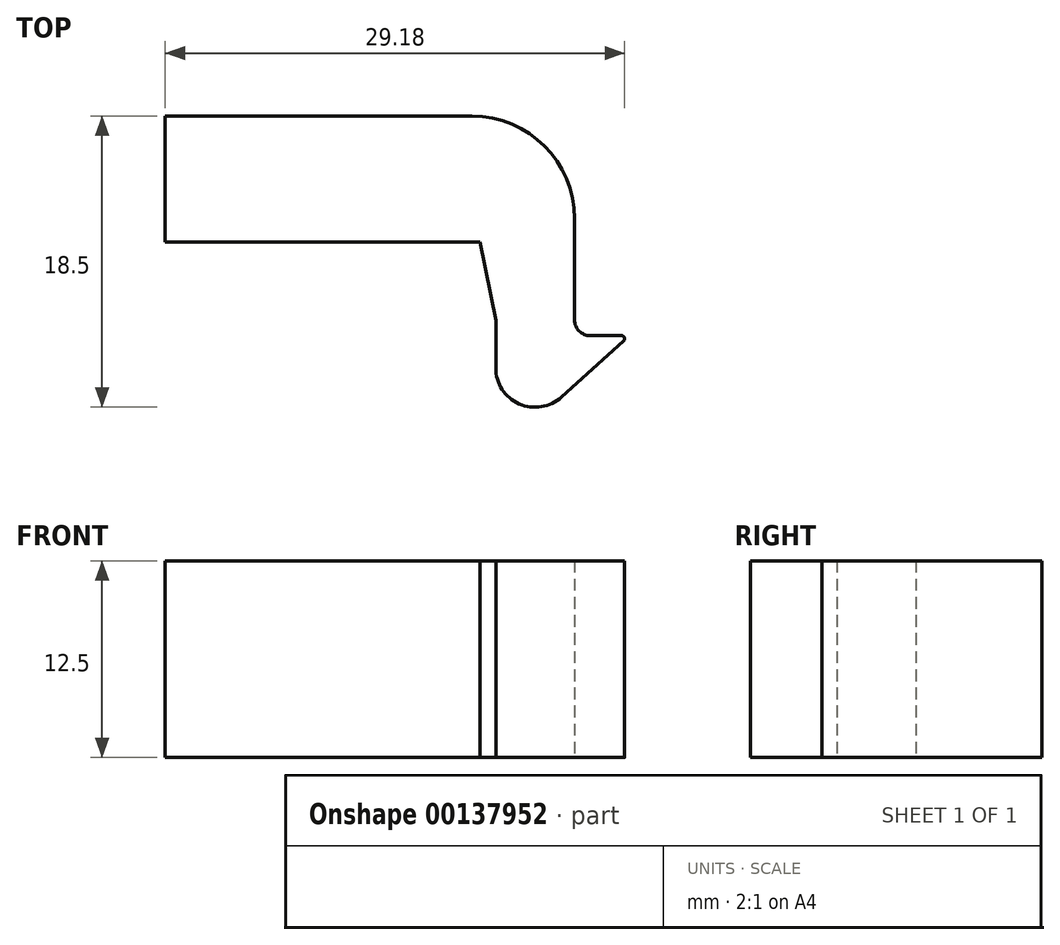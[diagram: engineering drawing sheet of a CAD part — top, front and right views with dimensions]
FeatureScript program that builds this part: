
annotation { "Feature Type Name" : "Feature", "Feature Type Description" : "" }
export const myFeature = defineFeature(function(context is Context, id is Id, definition is map)
    precondition{}
    {
        {
            var Q0;
            Q0=qCreatedBy(makeId("Top.planeOp"),FACE);
            var sketch = newSketch(context, id + "F0", { "sketchPlane" : qUnion([Q0])});
            skLineSegment(sketch, "E0.bottom", {"start": v(0, 0) * mm, "end": v(20, 0) * mm});
            skLineSegment(sketch, "E0.top", {"start": v(0, 8) * mm, "end": v(19.49, 8) * mm});
            skLineSegment(sketch, "E0.left", {"start": v(0, 0) * mm, "end": v(0, 8) * mm});
            skLineSegment(sketch, "E1", {"start": v(20, 0) * mm, "end": v(21, -5) * mm});
            skLineSegment(sketch, "E2", {"start": v(21, -5) * mm, "end": v(21, -8) * mm});
            skLineSegment(sketch, "E3", {"start": v(21, -8) * mm, "end": v(26, -8) * mm, "construction": true});
            skArc(sketch, "E4", {"start": v(21, -8) * mm, "mid": v(22.48, -10.28) * mm, "end": v(25.18, -9.86) * mm});
            skLineSegment(sketch, "E5", {"start": v(25.18, -9.86) * mm, "end": v(29.11, -6.3) * mm});
            skLineSegment(sketch, "E6", {"start": v(23.5, -10.5) * mm, "end": v(29.5, -10.5) * mm, "construction": true});
            skLineSegment(sketch, "E7", {"start": v(28.98, -5.95) * mm, "end": v(27, -5.95) * mm});
            skLineSegment(sketch, "E8", {"start": v(26, -4.95) * mm, "end": v(26, 1.49) * mm});
            skArc(sketch, "E9", {"start": v(19.49, 8) * mm, "mid": v(24.1, 6.1) * mm, "end": v(26, 1.49) * mm});
            skPoint(sketch, "E10.visualSharp", {"position": v(26, -5.95) * mm});
            skArc(sketch, "E10.filletArc", {"start": v(26, -4.95) * mm, "mid": v(26.3, -5.66) * mm, "end": v(27, -5.95) * mm});
            skPoint(sketch, "E11.visualSharp", {"position": v(29.5, -5.95) * mm});
            skArc(sketch, "E11.filletArc", {"start": v(29.11, -6.3) * mm, "mid": v(29.17, -6.08) * mm, "end": v(28.98, -5.95) * mm});
            skSolve(sketch);
        }
        {
            var Q0;
            Q0=makeQuery(id+"F0.imprint","IMPRINT",FACE,{"disambiguationData":[TD([[makeQuery(id+"F0.imprint","IMPRINT",EDGE,{"derivedFrom":sQuery(id+"F0.wireOp",EDGE,"E0.bottom")}),1.0]])]});
            extrude(context, id + "F1", {"entities" : qUnion([Q0]), "depth" : 12.5 * mm});
        }
    });
